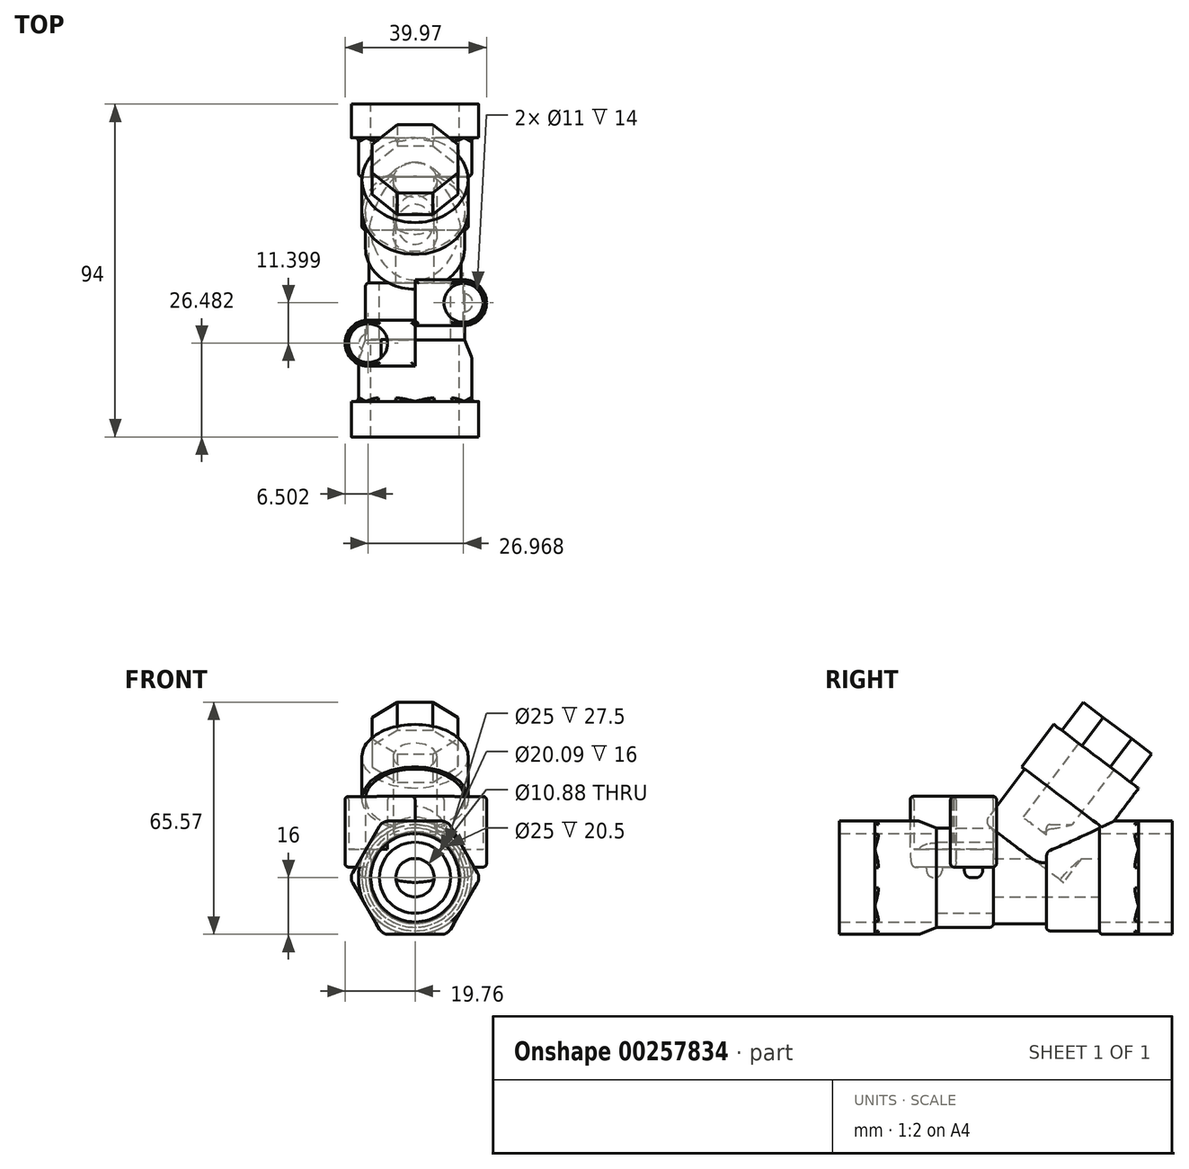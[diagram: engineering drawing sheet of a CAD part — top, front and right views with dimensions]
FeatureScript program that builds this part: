
annotation { "Feature Type Name" : "Feature", "Feature Type Description" : "" }
export const myFeature = defineFeature(function(context is Context, id is Id, definition is map)
    precondition{}
    {
        {
            var Q0;
            Q0=qCreatedBy(makeId("Front.planeOp"),FACE);
            var sketch = newSketch(context, id + "F0", { "sketchPlane" : qUnion([Q0])});
            skCircle(sketch, "E0", {"center": v(0, 0) * mm, "radius": 12.5 * mm});
            skCircle(sketch, "E1.cCircle", {"center": v(0, 0) * mm, "radius": 16 * mm, "construction": true});
            skLineSegment(sketch, "E1.0", {"start": v(-7.5, 16) * mm, "end": v(7.5, 16) * mm});
            skLineSegment(sketch, "E1.1", {"start": v(10.1, 14.5) * mm, "end": v(17.6, 1.5) * mm});
            skLineSegment(sketch, "E1.2", {"start": v(17.6, -1.5) * mm, "end": v(10.1, -14.5) * mm});
            skLineSegment(sketch, "E1.3", {"start": v(7.5, -16) * mm, "end": v(-7.5, -16) * mm});
            skLineSegment(sketch, "E1.4", {"start": v(-10.1, -14.5) * mm, "end": v(-17.6, -1.5) * mm});
            skLineSegment(sketch, "E1.5", {"start": v(-17.6, 1.5) * mm, "end": v(-10.1, 14.5) * mm});
            skPoint(sketch, "E1.0.midPoint", {"position": v(0, 16) * mm});
            skPoint(sketch, "E2.visualSharp", {"position": v(-9.24, 16) * mm});
            skArc(sketch, "E2.filletArc", {"start": v(-7.5, 16) * mm, "mid": v(-9, 15.6) * mm, "end": v(-10.1, 14.5) * mm});
            skPoint(sketch, "E3.visualSharp", {"position": v(9.24, 16) * mm});
            skArc(sketch, "E3.filletArc", {"start": v(10.1, 14.5) * mm, "mid": v(9, 15.6) * mm, "end": v(7.5, 16) * mm});
            skPoint(sketch, "E4.visualSharp", {"position": v(18.48, 0) * mm});
            skArc(sketch, "E4.filletArc", {"start": v(17.6, -1.5) * mm, "mid": v(18.01, 0) * mm, "end": v(17.6, 1.5) * mm});
            skPoint(sketch, "E5.visualSharp", {"position": v(9.24, -16) * mm});
            skArc(sketch, "E5.filletArc", {"start": v(7.5, -16) * mm, "mid": v(9, -15.6) * mm, "end": v(10.1, -14.5) * mm});
            skPoint(sketch, "E6.visualSharp", {"position": v(-9.24, -16) * mm});
            skArc(sketch, "E6.filletArc", {"start": v(-10.1, -14.5) * mm, "mid": v(-9, -15.6) * mm, "end": v(-7.5, -16) * mm});
            skPoint(sketch, "E7.visualSharp", {"position": v(-18.48, 0) * mm});
            skArc(sketch, "E7.filletArc", {"start": v(-17.6, 1.5) * mm, "mid": v(-18.01, 0) * mm, "end": v(-17.6, -1.5) * mm});
            skSolve(sketch);
        }
        {
            var Q0;
            Q0 = qSketchRegion(id + "F0", true);
            extrude(context, id + "F1", {"entities" : qUnion([Q0]), "depth" : 9.5 * mm});
        }
        {
            var Q0;
            Q0=makeQuery(id+"F1.opExtrude","CAP_FACE",FACE,{"disambiguationData":[OSD([sQuery(id+"F0.wireOp",EDGE,"E0"),sQuery(id+"F0.wireOp",EDGE,"E1.0"),sQuery(id+"F0.wireOp",EDGE,"E1.1"),sQuery(id+"F0.wireOp",EDGE,"E1.2"),sQuery(id+"F0.wireOp",EDGE,"E1.3"),sQuery(id+"F0.wireOp",EDGE,"E1.4"),sQuery(id+"F0.wireOp",EDGE,"E1.5"),sQuery(id+"F0.wireOp",EDGE,"E2.filletArc"),sQuery(id+"F0.wireOp",EDGE,"E3.filletArc"),sQuery(id+"F0.wireOp",EDGE,"E4.filletArc"),sQuery(id+"F0.wireOp",EDGE,"E5.filletArc"),sQuery(id+"F0.wireOp",EDGE,"E6.filletArc"),sQuery(id+"F0.wireOp",EDGE,"E7.filletArc")])],"isStart":false});
            var sketch = newSketch(context, id + "F2", { "sketchPlane" : qUnion([Q0])});
            skCircle(sketch, "E8", {"center": v(0, 0) * mm, "radius": 16 * mm});
            skCircle(sketch, "E9", {"center": v(0, 0) * mm, "radius": 12.5 * mm});
            skSolve(sketch);
        }
        {
            var Q0;
            Q0 = qSketchRegion(id + "F2", true);
            extrude(context, id + "F3", {"entities" : qUnion([Q0]), "operationType" : NewBodyOperationType.ADD, "depth" : 11 * mm});
        }
        {
            var Q0;
            Q0=makeQuery(id+"F3.opExtrude","CAP_FACE",FACE,{"disambiguationData":[OSD([sQuery(id+"F2.wireOp",EDGE,"E8"),sQuery(id+"F2.wireOp",EDGE,"E9")])],"isStart":false});
            var sketch = newSketch(context, id + "F4", { "sketchPlane" : qUnion([Q0])});
            skCircle(sketch, "E10", {"center": v(0, 0) * mm, "radius": 15 * mm});
            skCircle(sketch, "E11", {"center": v(0, 0) * mm, "radius": 5.44 * mm});
            skSolve(sketch);
        }
        {
            var Q0;
            Q0 = qSketchRegion(id + "F4", true);
            extrude(context, id + "F5", {"entities" : qUnion([Q0]), "operationType" : NewBodyOperationType.ADD, "depth" : 15 * mm});
        }
        {
            var Q0;
            Q0=makeQuery(id+"F5.opExtrude","CAP_FACE",FACE,{"disambiguationData":[OSD([sQuery(id+"F4.wireOp",EDGE,"E10"),sQuery(id+"F4.wireOp",EDGE,"E11")])],"isStart":false});
            var sketch = newSketch(context, id + "F6", { "sketchPlane" : qUnion([Q0])});
            skCircle(sketch, "E12", {"center": v(0, 0) * mm, "radius": 5.44 * mm});
            skCircle(sketch, "E13", {"center": v(0, 0) * mm, "radius": 13 * mm});
            skSolve(sketch);
        }
        {
            var Q0;
            Q0 = qSketchRegion(id + "F6", true);
            extrude(context, id + "F7", {"entities" : qUnion([Q0]), "operationType" : NewBodyOperationType.ADD, "depth" : 15 * mm});
        }
        {
            var Q0;
            Q0=makeQuery(id+"F7.opExtrude","CAP_FACE",FACE,{"disambiguationData":[OSD([sQuery(id+"F6.wireOp",EDGE,"E12"),sQuery(id+"F6.wireOp",EDGE,"E13")])],"isStart":false});
            var sketch = newSketch(context, id + "F8", { "sketchPlane" : qUnion([Q0])});
            skCircle(sketch, "E14", {"center": v(0, 0) * mm, "radius": 14 * mm});
            skCircle(sketch, "E15", {"center": v(0, 0) * mm, "radius": 10.04 * mm});
            skSolve(sketch);
        }
        {
            var Q0;
            Q0 = qSketchRegion(id + "F8", true);
            extrude(context, id + "F9", {"entities" : qUnion([Q0]), "operationType" : NewBodyOperationType.ADD, "depth" : 16 * mm});
        }
        {
            var Q0;
            Q0=makeQuery(id+"F9.opExtrude","CAP_FACE",FACE,{"disambiguationData":[OSD([sQuery(id+"F8.wireOp",EDGE,"E14"),sQuery(id+"F8.wireOp",EDGE,"E15")])],"isStart":false});
            var sketch = newSketch(context, id + "F10", { "sketchPlane" : qUnion([Q0])});
            skCircle(sketch, "E16", {"center": v(0, 0) * mm, "radius": 16 * mm});
            skCircle(sketch, "E17", {"center": v(0, 0) * mm, "radius": 12.5 * mm});
            skSolve(sketch);
        }
        {
            var Q0;
            Q0 = qSketchRegion(id + "F10", true);
            extrude(context, id + "F11", {"entities" : qUnion([Q0]), "operationType" : NewBodyOperationType.ADD, "depth" : 17.5 * mm});
        }
        {
            var Q0;
            Q0=makeQuery(id+"F11.opExtrude","CAP_FACE",FACE,{"disambiguationData":[OSD([sQuery(id+"F10.wireOp",EDGE,"E16"),sQuery(id+"F10.wireOp",EDGE,"E17")])],"isStart":false});
            var sketch = newSketch(context, id + "F12", { "sketchPlane" : qUnion([Q0])});
            skCircle(sketch, "E18", {"center": v(0, 0) * mm, "radius": 12.5 * mm});
            skCircle(sketch, "E19.cCircle", {"center": v(0, 0) * mm, "radius": 16 * mm, "construction": true});
            skLineSegment(sketch, "E19.0", {"start": v(-7.5, 16) * mm, "end": v(7.5, 16) * mm});
            skLineSegment(sketch, "E19.1", {"start": v(10.1, 14.5) * mm, "end": v(17.6, 1.5) * mm});
            skLineSegment(sketch, "E19.2", {"start": v(17.6, -1.5) * mm, "end": v(10.1, -14.5) * mm});
            skLineSegment(sketch, "E19.3", {"start": v(7.5, -16) * mm, "end": v(-7.5, -16) * mm});
            skLineSegment(sketch, "E19.4", {"start": v(-10.1, -14.5) * mm, "end": v(-17.6, -1.5) * mm});
            skLineSegment(sketch, "E19.5", {"start": v(-17.6, 1.5) * mm, "end": v(-10.1, 14.5) * mm});
            skPoint(sketch, "E19.0.midPoint", {"position": v(0, 16) * mm});
            skPoint(sketch, "E20.visualSharp", {"position": v(-9.24, 16) * mm});
            skArc(sketch, "E20.filletArc", {"start": v(-7.5, 16) * mm, "mid": v(-9, 15.6) * mm, "end": v(-10.1, 14.5) * mm});
            skPoint(sketch, "E21.visualSharp", {"position": v(9.24, 16) * mm});
            skArc(sketch, "E21.filletArc", {"start": v(10.1, 14.5) * mm, "mid": v(9, 15.6) * mm, "end": v(7.5, 16) * mm});
            skPoint(sketch, "E22.visualSharp", {"position": v(18.48, 0) * mm});
            skArc(sketch, "E22.filletArc", {"start": v(17.6, -1.5) * mm, "mid": v(18.01, 0) * mm, "end": v(17.6, 1.5) * mm});
            skPoint(sketch, "E23.visualSharp", {"position": v(9.24, -16) * mm});
            skArc(sketch, "E23.filletArc", {"start": v(7.5, -16) * mm, "mid": v(9, -15.6) * mm, "end": v(10.1, -14.5) * mm});
            skPoint(sketch, "E24.visualSharp", {"position": v(-9.24, -16) * mm});
            skArc(sketch, "E24.filletArc", {"start": v(-10.1, -14.5) * mm, "mid": v(-9, -15.6) * mm, "end": v(-7.5, -16) * mm});
            skPoint(sketch, "E25.visualSharp", {"position": v(-18.48, 0) * mm});
            skArc(sketch, "E25.filletArc", {"start": v(-17.6, 1.5) * mm, "mid": v(-18.01, 0) * mm, "end": v(-17.6, -1.5) * mm});
            skSolve(sketch);
        }
        {
            var Q0;
            Q0 = qSketchRegion(id + "F12", true);
            extrude(context, id + "F13", {"entities" : qUnion([Q0]), "operationType" : NewBodyOperationType.ADD, "depth" : 10 * mm});
        }
        {
            var Q0;
            Q0=makeQuery(id+"F11.opExtrude","CAP_EDGE",EDGE,{"disambiguationData":[OSD([sQuery(id+"F10.wireOp",EDGE,"E16")])],"isStart":true});
            chamfer(context, id + "F14", {"entities" : qUnion([Q0]), "chamferType" : ChamferType.OFFSET_ANGLE, "width" : 5 * mm, "oppositeDirection" : false, "angle" : 22.1 * degree, "tangentPropagation" : true});
        }
        {
            var Q0;
            Q0=makeQuery(id+"F9.opExtrude","CAP_EDGE",EDGE,{"disambiguationData":[OSD([sQuery(id+"F8.wireOp",EDGE,"E14")])],"isStart":true});
            var Q1;
            Q1=makeQuery(id+"F5.opExtrude","CAP_EDGE",EDGE,{"disambiguationData":[OSD([sQuery(id+"F4.wireOp",EDGE,"E10")])],"isStart":false});
            var Q2;
            Q2=makeQuery(id+"F3.opExtrude","CAP_EDGE",EDGE,{"disambiguationData":[OSD([sQuery(id+"F2.wireOp",EDGE,"E8")])],"isStart":false});
            var Q3;
            Q3=makeQuery(id+"F3.opExtrude","SWEPT_FACE",FACE,{"disambiguationData":[OSD([sQuery(id+"F2.wireOp",EDGE,"E8")])]});
            var Q4;
            Q4=makeQuery(id+"F11.opExtrude","SWEPT_FACE",FACE,{"disambiguationData":[OSD([sQuery(id+"F10.wireOp",EDGE,"E16")])]});
            fillet(context, id + "F15", {"entities" : qUnion([Q0, Q1, Q2, Q3, Q4]), "radius" : 1 * mm, "tangentPropagation" : true, "allowEdgeOverflow" : false});
        }
        {
            var Q0;
            Q0=qCreatedBy(makeId("Top.planeOp"),FACE);
            var sketch = newSketch(context, id + "F16", { "sketchPlane" : qUnion([Q0])});
            skCircle(sketch, "E26", {"center": v(-13.26, -67.52) * mm, "radius": 2.58 * mm});
            skCircle(sketch, "E27", {"center": v(13.71, -56.12) * mm, "radius": 2.58 * mm});
            skSolve(sketch);
        }
        {
            var Q0;
            Q0 = qSketchRegion(id + "F16", true);
            extrude(context, id + "F17", {"entities" : qUnion([Q0]), "operationType" : NewBodyOperationType.ADD, "depth" : 3 * mm});
        }
        {
            var Q0;
            Q0=makeQuery(id+"F17.opExtrude","CAP_EDGE",EDGE,{"disambiguationData":[OSD([sQuery(id+"F16.wireOp",EDGE,"E27")])],"isStart":true});
            var Q1;
            {var subQ0=sQuery(id+"F16.wireOp",EDGE,"E26");Q1=makeQuery(id+"F17.boolean.opBoolean","SPLIT",EDGE,{"disambiguationData":[TD([makeQuery(id+"F9.opExtrude","SWEPT_FACE",FACE,{"disambiguationData":[OSD([sQuery(id+"F8.wireOp",EDGE,"E14")])]})])],"derivedFrom":makeQuery(id+"F17.opExtrude","CAP_EDGE",EDGE,{"disambiguationData":[OSD([subQ0])],"isStart":true})});}
            fillet(context, id + "F18", {"entities" : qUnion([Q0, Q1]), "radius" : 2 * mm, "tangentPropagation" : true, "allowEdgeOverflow" : false});
        }
        {
            var Q0;
            {var subQ0=sQuery(id+"F16.wireOp",EDGE,"E26");Q0=makeQuery(id+"F17.boolean.opBoolean","SPLIT",FACE,{"disambiguationData":[TD([makeQuery(id+"F9.opExtrude","SWEPT_FACE",FACE,{"disambiguationData":[OSD([sQuery(id+"F8.wireOp",EDGE,"E14")])]})])],"derivedFrom":makeQuery(id+"F17.opExtrude","CAP_FACE",FACE,{"disambiguationData":[OSD([subQ0])],"isStart":false})});}
            var sketch = newSketch(context, id + "F19", { "sketchPlane" : qUnion([Q0])});
            skCircle(sketch, "E28", {"center": v(-13.26, -67.52) * mm, "radius": 5.5 * mm});
            skCircle(sketch, "E29", {"center": v(13.71, -56.12) * mm, "radius": 5.5 * mm});
            skCircle(sketch, "E30", {"center": v(-13.26, -67.52) * mm, "radius": 6.5 * mm});
            skCircle(sketch, "E31", {"center": v(13.71, -56.12) * mm, "radius": 6.5 * mm});
            skLineSegment(sketch, "E32", {"start": v(-13.26, -61.02) * mm, "end": v(0, -61.02) * mm});
            skLineSegment(sketch, "E33", {"start": v(-13.26, -74.02) * mm, "end": v(0, -74.02) * mm});
            skLineSegment(sketch, "E34", {"start": v(13.71, -49.62) * mm, "end": v(0, -49.62) * mm});
            skLineSegment(sketch, "E35", {"start": v(0, -49.62) * mm, "end": v(0, -61.02) * mm});
            skLineSegment(sketch, "E36", {"start": v(13.71, -62.62) * mm, "end": v(0, -62.62) * mm});
            skLineSegment(sketch, "E37", {"start": v(0, -62.62) * mm, "end": v(0, -74.02) * mm});
            skSolve(sketch);
        }
        {
            var Q0;
            Q0 = qSketchRegion(id + "F19", true);
            extrude(context, id + "F20", {"entities" : qUnion([Q0]), "operationType" : NewBodyOperationType.ADD, "depth" : 20 * mm});
        }
        {
            var Q0;
            {var subQ0=sQuery(id+"F19.wireOp",EDGE,"E28");var subQ1=sQuery(id+"F19.wireOp",EDGE,"E30");Q0=makeQuery(id+"F20.boolean.opBoolean","SPLIT",FACE,{"disambiguationData":[TD([makeQuery(id+"F11.opExtrude","SWEPT_FACE",FACE,{"disambiguationData":[OSD([sQuery(id+"F10.wireOp",EDGE,"E16")])]})])],"derivedFrom":makeQuery(id+"F20.opExtrude","CAP_FACE",FACE,{"disambiguationData":[OSD([subQ0,sQuery(id+"F19.wireOp",EDGE,"E29"),subQ1,sQuery(id+"F19.wireOp",EDGE,"E31"),sQuery(id+"F19.wireOp",EDGE,"E32"),sQuery(id+"F19.wireOp",EDGE,"E33"),sQuery(id+"F19.wireOp",EDGE,"LPEtJJ2H-jGcg-WLoc-efmV-Qcx0MSgyULsx"),sQuery(id+"F19.wireOp",EDGE,"s637VcAT-8eYg-yXFH-sKqK-25iUyspzpOhs"),sQuery(id+"F19.wireOp",EDGE,"E34"),sQuery(id+"F19.wireOp",EDGE,"E35")])],"isStart":true})});}
            var sketch = newSketch(context, id + "F21", { "sketchPlane" : qUnion([Q0])});
            skCircle(sketch, "E38", {"center": v(-13.26, 67.52) * mm, "radius": 5.5 * mm});
            skCircle(sketch, "E39", {"center": v(13.71, 56.12) * mm, "radius": 5.5 * mm});
            skSolve(sketch);
        }
        {
            var Q0;
            Q0 = qSketchRegion(id + "F21", true);
            extrude(context, id + "F22", {"entities" : qUnion([Q0]), "operationType" : NewBodyOperationType.ADD, "oppositeDirection" : true, "depth" : 5 * mm});
        }
        {
            var Q0;
            Q0=makeQuery(id+"F20.opExtrude","CAP_EDGE",EDGE,{"disambiguationData":[OSD([sQuery(id+"F19.wireOp",EDGE,"E31")])],"isStart":true});
            var Q1;
            Q1=makeQuery(id+"F20.opExtrude","CAP_EDGE",EDGE,{"disambiguationData":[OSD([sQuery(id+"F19.wireOp",EDGE,"E30")])],"isStart":true});
            var Q2;
            Q2=makeQuery(id+"F20.opExtrude","CAP_FACE",FACE,{"disambiguationData":[OSD([sQuery(id+"F19.wireOp",EDGE,"E28"),sQuery(id+"F19.wireOp",EDGE,"E29"),sQuery(id+"F19.wireOp",EDGE,"E30"),sQuery(id+"F19.wireOp",EDGE,"E31"),sQuery(id+"F19.wireOp",EDGE,"E32"),sQuery(id+"F19.wireOp",EDGE,"E33"),sQuery(id+"F19.wireOp",EDGE,"LPEtJJ2H-jGcg-WLoc-efmV-Qcx0MSgyULsx"),sQuery(id+"F19.wireOp",EDGE,"s637VcAT-8eYg-yXFH-sKqK-25iUyspzpOhs"),sQuery(id+"F19.wireOp",EDGE,"E34"),sQuery(id+"F19.wireOp",EDGE,"E35")])],"isStart":false});
            fillet(context, id + "F23", {"entities" : qUnion([Q0, Q1, Q2]), "radius" : 1 * mm, "tangentPropagation" : true, "allowEdgeOverflow" : false});
        }
        {
            var Q0;
            Q0=makeQuery(id+"F7.opExtrude","CAP_FACE",FACE,{"disambiguationData":[OSD([sQuery(id+"F6.wireOp",EDGE,"E12"),sQuery(id+"F6.wireOp",EDGE,"E13")])],"isStart":false});
            var sketch = newSketch(context, id + "F24", { "sketchPlane" : qUnion([Q0])});
            skCircle(sketch, "E40", {"center": v(0, 0) * mm, "radius": 10.04 * mm});
            skSolve(sketch);
        }
        {
            var Q0;
            Q0 = qSketchRegion(id + "F24", true);
            extrude(context, id + "F25", {"entities" : qUnion([Q0]), "operationType" : NewBodyOperationType.REMOVE, "depth" : 25 * mm});
        }
        {
            var Q0;
            {var subQ0=sQuery(id+"F16.wireOp",EDGE,"E26");var subQ1=sQuery(id+"F8.wireOp",EDGE,"E15");Q0=makeQuery(id+"F22.boolean.opBoolean","SPLIT",FACE,{"disambiguationData":[TD([makeQuery(id+"F17.opExtrude","SWEPT_FACE",FACE,{"disambiguationData":[OSD([subQ0])]})])],"derivedFrom":makeQuery(id+"F9.opExtrude","CAP_FACE",FACE,{"disambiguationData":[OSD([sQuery(id+"F8.wireOp",EDGE,"E14"),subQ1])],"isStart":false})});}
            var sketch = newSketch(context, id + "F26", { "sketchPlane" : qUnion([Q0])});
            skCircle(sketch, "E41", {"center": v(0, 0) * mm, "radius": 12.5 * mm});
            skSolve(sketch);
        }
        {
            var Q0;
            Q0 = qSketchRegion(id + "F26", true);
            extrude(context, id + "F27", {"entities" : qUnion([Q0]), "operationType" : NewBodyOperationType.REMOVE, "depth" : 25 * mm});
        }
        {
            var Q0;
            Q0=makeQuery(id+"F25.boolean.opBoolean","MERGE",FACE,{"derivedFrom":[makeQuery(id+"F7.opExtrude","CAP_FACE",FACE,{"disambiguationData":[OSD([sQuery(id+"F6.wireOp",EDGE,"E12"),sQuery(id+"F6.wireOp",EDGE,"E13")])],"isStart":false}),makeQuery(id+"F25.opExtrude","CAP_FACE",FACE,{"disambiguationData":[OSD([sQuery(id+"F24.wireOp",EDGE,"E40")])],"isStart":true})]});
            var sketch = newSketch(context, id + "F28", { "sketchPlane" : qUnion([Q0])});
            skCircle(sketch, "E42", {"center": v(0, 0) * mm, "radius": 5.44 * mm});
            skSolve(sketch);
        }
        {
            var Q0;
            Q0 = qSketchRegion(id + "F28", true);
            extrude(context, id + "F29", {"entities" : qUnion([Q0]), "operationType" : NewBodyOperationType.REMOVE, "oppositeDirection" : true, "depth" : 25 * mm});
        }
        {
            var Q0;
            Q0=makeQuery(id+"F22.boolean.opBoolean","SPLIT",FACE,{"disambiguationData":[TD([makeQuery(id+"F9.opExtrude","SWEPT_FACE",FACE,{"disambiguationData":[OSD([sQuery(id+"F8.wireOp",EDGE,"E14")])]})])],"derivedFrom":makeQuery(id+"F22.opExtrude","CAP_FACE",FACE,{"disambiguationData":[OSD([sQuery(id+"F21.wireOp",EDGE,"E38")])],"isStart":false})});
            var sketch = newSketch(context, id + "F30", { "sketchPlane" : qUnion([Q0])});
            skCircle(sketch, "E43", {"center": v(-13.26, -67.52) * mm, "radius": 5.5 * mm});
            skCircle(sketch, "E44", {"center": v(13.71, -56.12) * mm, "radius": 5.5 * mm});
            skSolve(sketch);
        }
        {
            var Q0;
            Q0 = qSketchRegion(id + "F30", true);
            extrude(context, id + "F31", {"entities" : qUnion([Q0]), "operationType" : NewBodyOperationType.REMOVE, "depth" : 25 * mm});
        }
        {
            var Q0;
            Q0=qCreatedBy(makeId("Right.planeOp"),FACE);
            var sketch = newSketch(context, id + "F32", { "sketchPlane" : qUnion([Q0])});
            skLineSegment(sketch, "E45", {"start": v(-72.65, -1.3) * mm, "end": v(-23.86, -1.3) * mm, "construction": true});
            skLineSegment(sketch, "E46", {"start": v(-48.25, -1.3) * mm, "end": v(-1.99, 60.1) * mm, "construction": true});
            skLineSegment(sketch, "E47", {"start": v(-53.08, 15.55) * mm, "end": v(-41.9, 7.13) * mm});
            skLineSegment(sketch, "E48", {"start": v(-53.08, 15.55) * mm, "end": v(-41.65, 30.72) * mm});
            skLineSegment(sketch, "E49", {"start": v(-41.9, 7.13) * mm, "end": v(-30.72, -1.3) * mm, "construction": true});
            skLineSegment(sketch, "E50", {"start": v(-30.72, -1.3) * mm, "end": v(-19.29, 13.87) * mm, "construction": true});
            skLineSegment(sketch, "E51.0", {"start": v(-42.16, 17.09) * mm, "end": v(-37.2, 13.35) * mm});
            skLineSegment(sketch, "E51.1", {"start": v(-42.16, 17.09) * mm, "end": v(-35.42, 26.03) * mm});
            skLineSegment(sketch, "E52", {"start": v(-37.2, 13.35) * mm, "end": v(-41.9, 7.13) * mm});
            skLineSegment(sketch, "E53", {"start": v(-35.42, 26.03) * mm, "end": v(-41.65, 30.72) * mm});
            skSolve(sketch);
        }
        {
            var Q0;
            Q0=makeQuery(id+"F32.imprint","IMPRINT",FACE,{"disambiguationData":[TD([[makeQuery(id+"F32.imprint","IMPRINT",EDGE,{"derivedFrom":sQuery(id+"F32.wireOp",EDGE,"E47")}),1.0]])]});
            var Q1;
            Q1=sQuery(id+"F32.wireOp",EDGE,"E46");
            revolve(context, id + "F33", {"operationType" : NewBodyOperationType.ADD, "entities" : qUnion([Q0]), "axis" : qUnion([Q1]), "revolveType" : RevolveType.FULL});
        }
        {
            var Q0;
            {var subQ0=sQuery(id+"F32.wireOp",EDGE,"E47");var subQ1=sQuery(id+"F32.wireOp",EDGE,"E48");Q0=makeQuery(id+"F33.boolean.opBoolean","SPLIT",EDGE,{"disambiguationData":[TD([makeQuery(id+"F20.opExtrude","SWEPT_FACE",FACE,{"disambiguationData":[OSD([sQuery(id+"F19.wireOp",EDGE,"E34")])]})])],"derivedFrom":makeQuery(id+"F33.opRevolve","SWEPT_EDGE",EDGE,{"disambiguationData":[OSD([subQ0,subQ1])]})});}
            var Q1;
            {var subQ0=sQuery(id+"F32.wireOp",EDGE,"E47");var subQ1=sQuery(id+"F32.wireOp",EDGE,"E48");Q1=makeQuery(id+"F33.boolean.opBoolean","SPLIT",EDGE,{"disambiguationData":[TD([makeQuery(id+"F20.opExtrude","SWEPT_FACE",FACE,{"disambiguationData":[OSD([sQuery(id+"F19.wireOp",EDGE,"E35")])]})])],"derivedFrom":makeQuery(id+"F33.opRevolve","SWEPT_EDGE",EDGE,{"disambiguationData":[OSD([subQ0,subQ1])]})});}
            fillet(context, id + "F34", {"entities" : qUnion([Q0, Q1]), "radius" : 2 * mm, "tangentPropagation" : true, "allowEdgeOverflow" : false});
        }
        {
            var Q0;
            Q0=makeQuery(id+"F33.opRevolve","SWEPT_FACE",FACE,{"disambiguationData":[OSD([sQuery(id+"F32.wireOp",EDGE,"E53")])]});
            var sketch = newSketch(context, id + "F35", { "sketchPlane" : qUnion([Q0])});
            skCircle(sketch, "E54", {"center": v(0, -37.75) * mm, "radius": 15 * mm});
            skCircle(sketch, "E55", {"center": v(0, -37.75) * mm, "radius": 6.2 * mm});
            skSolve(sketch);
        }
        {
            var Q0;
            Q0 = qSketchRegion(id + "F35", true);
            extrude(context, id + "F36", {"entities" : qUnion([Q0]), "operationType" : NewBodyOperationType.ADD, "depth" : 15 * mm});
        }
        {
            var Q0;
            Q0=makeQuery(id+"F36.opExtrude","CAP_FACE",FACE,{"disambiguationData":[OSD([sQuery(id+"F35.wireOp",EDGE,"E54"),sQuery(id+"F35.wireOp",EDGE,"E55")])],"isStart":false});
            var sketch = newSketch(context, id + "F37", { "sketchPlane" : qUnion([Q0])});
            skCircle(sketch, "E56.cCircle", {"center": v(0, -37.75) * mm, "radius": 12.13 * mm, "construction": true});
            skLineSegment(sketch, "E56.0", {"start": v(5.03, -49.89) * mm, "end": v(-5.03, -49.89) * mm});
            skLineSegment(sketch, "E56.1", {"start": v(-5.03, -49.89) * mm, "end": v(-12.13, -42.78) * mm});
            skLineSegment(sketch, "E56.2", {"start": v(-12.13, -42.78) * mm, "end": v(-12.13, -32.73) * mm});
            skLineSegment(sketch, "E56.3", {"start": v(-12.13, -32.73) * mm, "end": v(-5.03, -25.62) * mm});
            skLineSegment(sketch, "E56.4", {"start": v(-5.03, -25.62) * mm, "end": v(5.03, -25.62) * mm});
            skLineSegment(sketch, "E56.5", {"start": v(5.03, -25.62) * mm, "end": v(12.13, -32.73) * mm});
            skLineSegment(sketch, "E56.6", {"start": v(12.13, -32.73) * mm, "end": v(12.13, -42.78) * mm});
            skLineSegment(sketch, "E56.7", {"start": v(12.13, -42.78) * mm, "end": v(5.03, -49.89) * mm});
            skPoint(sketch, "E56.0.midPoint", {"position": v(0, -49.89) * mm});
            skSolve(sketch);
        }
        {
            var Q0;
            Q0 = qSketchRegion(id + "F37", true);
            extrude(context, id + "F38", {"entities" : qUnion([Q0]), "operationType" : NewBodyOperationType.ADD, "depth" : 10 * mm});
        }
    });
